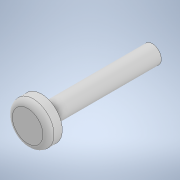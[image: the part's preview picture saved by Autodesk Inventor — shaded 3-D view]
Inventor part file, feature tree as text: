
AUTODESK INVENTOR PART (.ipt)
format: ipt  version: 2021 (Build 250183000, 183)  size: 121,856 bytes
history: native  units: in
note: dims shown in document units (in); Inventor stores cm internally (conversion verified against a paired STEP export)
features: revolve x1, fillet x1, sketch x1
ambient origin geometry x8: Origin, YZ Plane, XZ Plane, XY Plane, X Axis, Y Axis, Z Axis, Center Point
bodies: Solid1 (feature_tree)
feature tree (3):
  revolve  "Revolution1"  [1 undecoded]
  fillet  "Fillet1"  Radius=0.0591in
  sketch  "Sketch2"  dims[d0=0.0256in d1=0.1575in d2=0.0591in d3=0.0197in d4=90.0deg d5=0.0079in]
note: 1 required parameter value undecoded (feature->parameter linkage not recoverable at this tier; creation-order binding heuristic only, values carry confidence <= 0.55)
